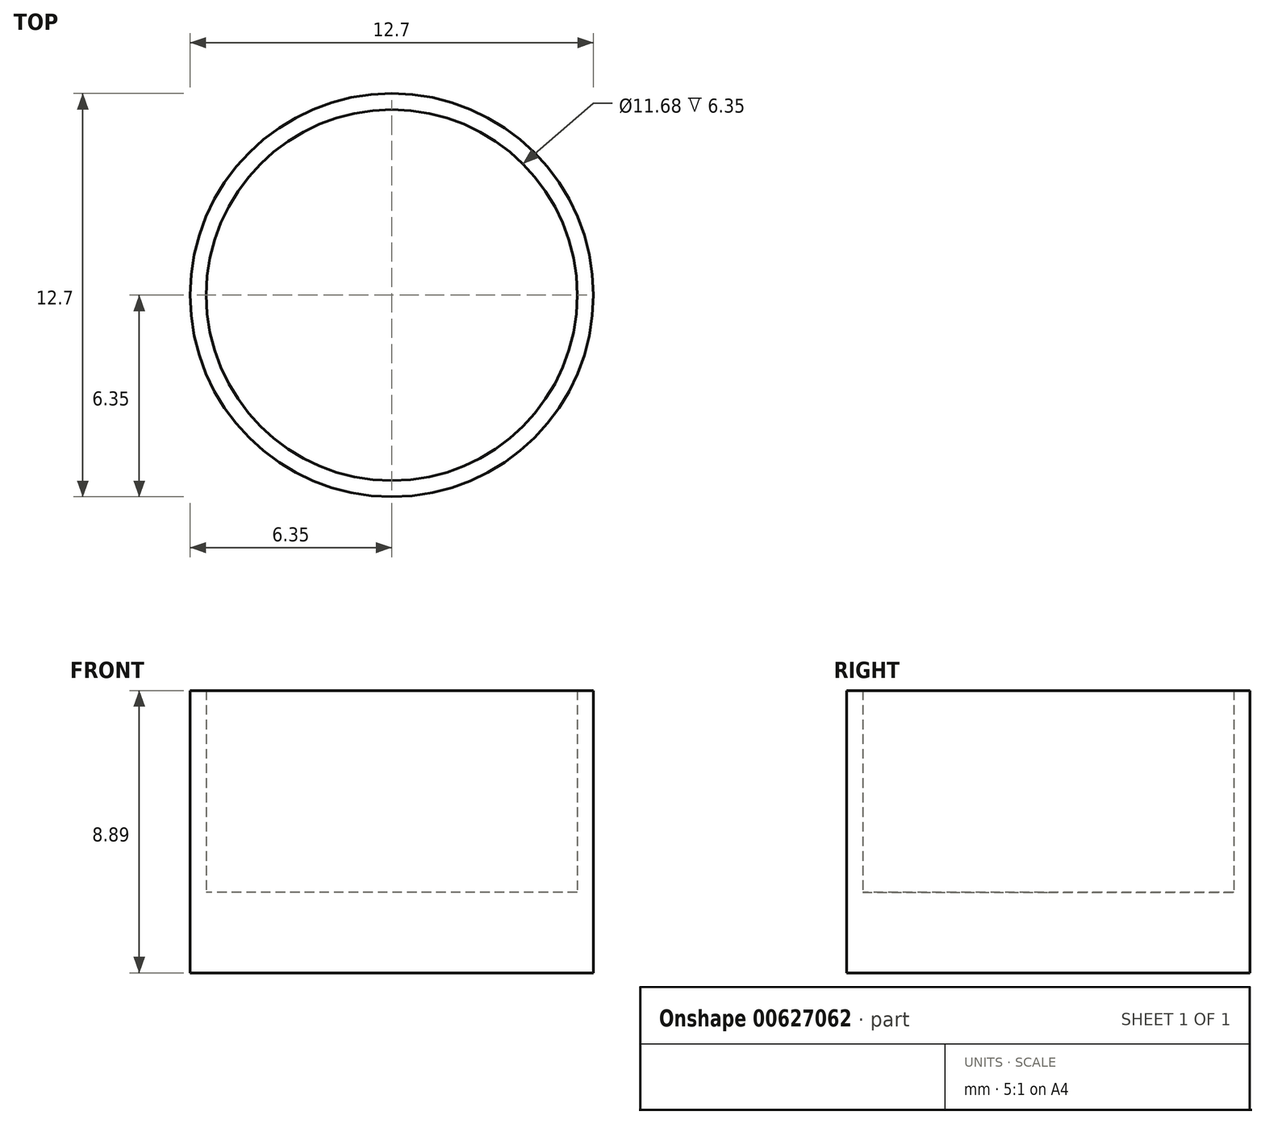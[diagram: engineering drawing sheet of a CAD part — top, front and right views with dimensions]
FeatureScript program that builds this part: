
annotation { "Feature Type Name" : "Feature", "Feature Type Description" : "" }
export const myFeature = defineFeature(function(context is Context, id is Id, definition is map)
    precondition{}
    {
        {
            var Q0;
            Q0=qCreatedBy(makeId("Top.planeOp"),FACE);
            var sketch = newSketch(context, id + "F0", { "sketchPlane" : qUnion([Q0])});
            skCircle(sketch, "E0", {"center": v(0, 0) * mm, "radius": 6.35 * mm});
            skCircle(sketch, "E1", {"center": v(0, 0) * mm, "radius": 5.84 * mm});
            skSolve(sketch);
        }
        {
            var Q0;
            Q0=makeQuery(id+"F0.imprint","IMPRINT",FACE,{"disambiguationData":[TD([[makeQuery(id+"F0.imprint","IMPRINT",EDGE,{"derivedFrom":sQuery(id+"F0.wireOp",EDGE,"E1")}),1.0]])]});
            var Q1;
            Q1=makeQuery(id+"F0.imprint","IMPRINT",FACE,{"disambiguationData":[TD([[makeQuery(id+"F0.imprint","IMPRINT",EDGE,{"derivedFrom":sQuery(id+"F0.wireOp",EDGE,"E0")}),1.0]])]});
            extrude(context, id + "F1", {"entities" : qUnion([Q0, Q1]), "depth" : 8.9 * mm, "offsetDistance" : 25.4 * mm});
        }
        {
            var Q0;
            Q0=makeQuery(id+"F0.imprint","IMPRINT",FACE,{"disambiguationData":[TD([[makeQuery(id+"F0.imprint","IMPRINT",EDGE,{"derivedFrom":sQuery(id+"F0.wireOp",EDGE,"E1")}),1.0]])]});
            extrude(context, id + "F2", {"entities" : qUnion([Q0]), "operationType" : NewBodyOperationType.REMOVE, "depth" : 25.4 * mm, "offsetDistance" : 25.4 * mm, "hasSecondDirection" : true, "secondDirectionOppositeDirection" : false, "secondDirectionDepth" : 2.54 * mm});
        }
    });
